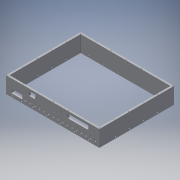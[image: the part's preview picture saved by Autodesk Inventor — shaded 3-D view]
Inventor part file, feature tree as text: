
AUTODESK INVENTOR PART (.ipt)
format: ipt  version: 2017 (Build 210142000, 142)  size: 591,360 bytes
history: native  units: in
note: dims shown in document units (in); Inventor stores cm internally (conversion verified against a paired STEP export)
features: hole x16, other x10, pattern_linear x10, fillet x8, extrude x4, projected_geometry x1, sketch x1
ambient origin geometry x8: Origin, YZ Plane, XZ Plane, XY Plane, X Axis, Y Axis, Z Axis, Center Point
bodies: Solid1 (feature_tree)
feature tree (50):
  extrude  "Extrusion1"  Depth=7.626in
  other  "left-2"
  other  "left-1"
  other  "bottom-1"
  hole  "Hole8"  [1 undecoded]
  hole  "Hole9"  [1 undecoded]
  other  "front-1"
  hole  "Hole10"  [1 undecoded]
  other  "right-1"
  hole  "Hole11"  [1 undecoded]
  hole  "Hole12"  [1 undecoded]
  pattern_linear  "Rectangular Pattern9"  Spacing1=0.0935in  [1 undecoded]
  pattern_linear  "Rectangular Pattern10"  Spacing1=0.0935in  [1 undecoded]
  pattern_linear  "Rectangular Pattern11"  Count1=6 Spacing1=1.562in
  pattern_linear  "Rectangular Pattern12"  Count1=7 Spacing1=1.635in
  hole  "Hole13"  [1 undecoded]
  hole  "Hole16"  [1 undecoded]
  hole  "Hole17"  [1 undecoded]
  extrude  "Extrusion2"  Depth=0.187in
  hole  "Hole18"  [1 undecoded]
  hole  "Hole19"  [1 undecoded]
  hole  "Hole20"  [1 undecoded]
  hole  "Hole21"  [1 undecoded]
  pattern_linear  "Rectangular Pattern13"  Spacing1=1.1693in  [1 undecoded]
  hole  "Hole22"  [1 undecoded]
  pattern_linear  "Rectangular Pattern14"  Spacing1=2.05in  [1 undecoded]
  pattern_linear  "Rectangular Pattern15"  Spacing1=0.41in  [1 undecoded]
  pattern_linear  "Rectangular Pattern16"  Spacing1=0.368in  [1 undecoded]
  pattern_linear  "Rectangular Pattern17"  Spacing1=1.0in  [1 undecoded]
  pattern_linear  "Rectangular Pattern19"  Spacing1=1.75in  [1 undecoded]
  fillet  "Fillet1"  Radius=0.185in
  fillet  "Fillet2"  Radius=1.0in
  fillet  "Fillet3"  Radius=0.185in
  fillet  "Fillet4"  Radius=0.185in
  fillet  "Fillet5"  Radius=1.75in
  fillet  "Fillet6"  Radius=0.185in
  fillet  "Fillet7"  Radius=0.3937in
  fillet  "Fillet8"  Radius=0.562in
  other  "dsub37"
  other  "dsub9"
  hole  "Hole_jackpost_dsub37"  [1 undecoded]
  extrude  "dsub37 cutout"  Depth=0.187in
  hole  "Hole_jackpost_dsub9"  [1 undecoded]
  extrude  "dsub9 cutout"  Depth=0.187in
  hole  "Hole26"  [1 undecoded]
  other  "Ext-Sketch"
  other  "back-1"
  other  "top"
  projected_geometry  "Projected Loop3"
  sketch  "Sketch30"  dims[d6=9.626in d8=7.626in d9=8.0in d10=10.0in d11=0.187in d12=0.187in d13=1.75in d14=0.0in d125=0.0935in d126=0.0935in d127=0.067in d128=0.2in d129=0.375in d130=0.25in d131=0.5635in d132=0.2in d133=0.8108in d134=2.3622in d136=1.562in d137=2.7559in d139=1.635in d140=0.0935in d141=0.0935in d142=0.067in d143=0.2in d144=0.375in d145=0.25in d146=0.5635in d147=0.2in d148=0.8108in d149=2.3622in d151=1.562in d152=2.7559in d154=1.635in d155=0.096in d156=0.75in d157=0.16in d158=0.25in d159=0.5635in d160=1.0in d161=0.8108in d162=0.096in d163=0.75in d164=0.16in d165=0.25in d166=0.5635in d167=1.0in d168=0.8108in d169=0.096in d170=0.75in d171=0.16in d172=0.25in d173=0.5635in d174=1.0in d175=0.8108in d176=0.095in d177=0.095in d180=0.067in d181=0.2in d182=0.375in d183=0.25in d184=0.5635in d185=0.2in d186=0.8108in d197=0.24in d203=0.48in d222=1.1693in d223=0.4094in d224=2.05in d225=0.41in d227=0.368in d238=0.067in d239=0.75in d240=0.375in d241=0.25in d242=0.5635in d243=1.0in d244=0.8108in d245=0.17in d246=0.75in d247=0.375in d248=0.25in d249=0.5635in d250=1.0in d251=0.8108in d252=1.0in d253=0.0in d254=1.75in d255=0.185in d256=1.0in d257=0.185in d259=0.185in d260=1.75in d261=0.185in d262=0.096in d263=0.75in d264=0.16in d265=0.25in d266=0.5635in d267=1.0in d268=0.8108in d271=6.2992in d273=0.5in d274=0.3937in d276=1.0in d278=0.17in d279=0.75in d280=0.375in d281=0.25in d282=0.5635in d283=1.0in d284=0.8108in d285=0.17in d286=0.75in d287=0.375in d288=0.25in d289=0.5635in d290=1.0in d291=0.8108in d292=0.067in d293=0.75in d294=0.375in d295=0.25in d296=0.5635in d297=0.2in d298=0.8108in d299=0.562in d300=2.05in d301=2.05in d302=0.65in d303=0.7874in d305=1.0in d306=0.25in d307=0.185in d308=0.096in d309=0.75in d310=0.16in d311=0.25in d312=0.5635in d313=1.0in d314=0.8108in d315=1.9685in d317=1.5in d318=2.3622in d320=1.6in d321=1.5748in d323=1.5in d324=1.5748in d326=1.5in d331=2.3622in d333=1.562in d334=2.7559in d336=1.635in d338=0.06in d339=0.06in d340=0.06in d341=0.06in d342=0.031in d343=0.031in d344=0.031in d345=0.031in d434=0.17in d477=2.3in d478=0.089in d479=0.089in d482=0.166in d483=0.166in d484=0.56in d486=0.984in d490=0.23in d491=0.44in d492=0.166in d493=0.166in d496=0.089in d497=1.038in d498=0.089in d499=2.5in d500=0.264in d501=0.264in d502=0.264in d503=0.264in d505=2.0in d506=0.132in d507=0.132in d508=0.132in d509=0.132in d510=0.21in d511=0.425in d515=0.085in d516=0.224in d517=0.375in d518=0.25in d519=0.5635in d520=0.187in d521=0.8108in d522=1.0in d523=0.0in d524=0.085in d525=0.224in d526=0.375in d527=0.25in d528=0.5635in d529=0.187in d530=0.8108in d531=1.0in d532=0.0in d537=0.085in d538=0.224in d539=0.375in d540=0.25in d541=0.5635in d542=0.187in d543=0.8108in d544=0.47in d545=0.47in d547=0.6871in d548=0.6871in d33=1.0in d34=1.0in d383=1.0in d384=1.0in]
note: 24 required parameter values undecoded (feature->parameter linkage not recoverable at this tier; creation-order binding heuristic only, values carry confidence <= 0.55)
